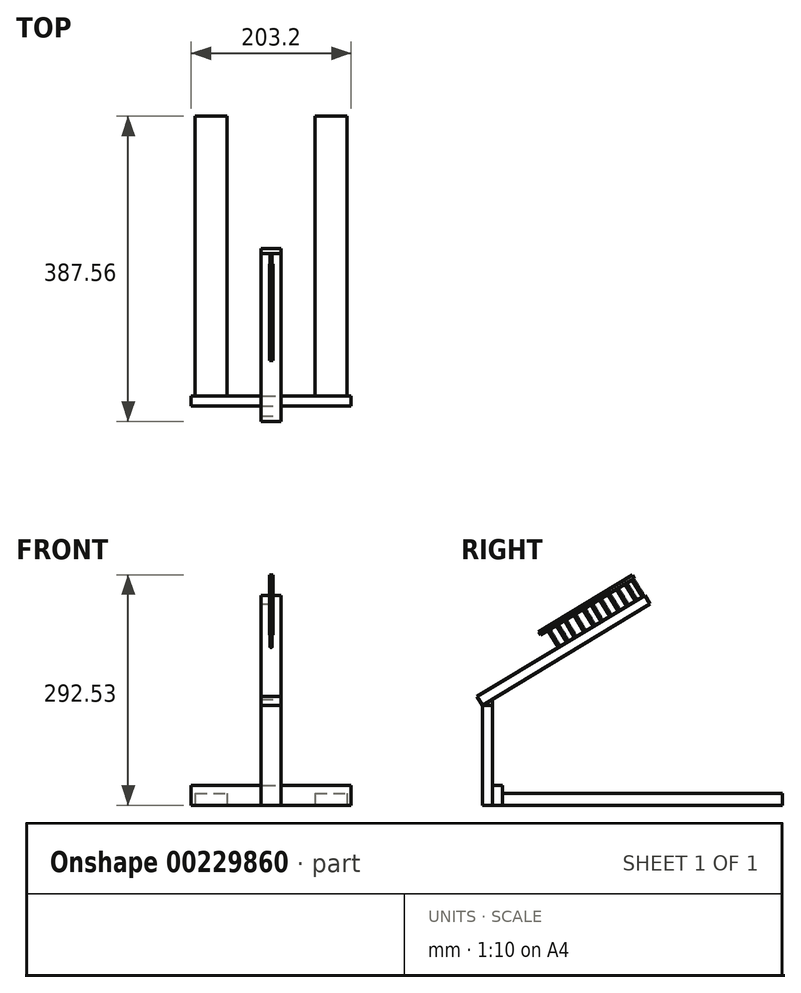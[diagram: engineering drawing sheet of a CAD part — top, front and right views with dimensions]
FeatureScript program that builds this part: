
annotation { "Feature Type Name" : "Feature", "Feature Type Description" : "" }
export const myFeature = defineFeature(function(context is Context, id is Id, definition is map)
    precondition{}
    {
        {
            var Q0;
            Q0=qCreatedBy(makeId("Top.planeOp"),FACE);
            var sketch = newSketch(context, id + "F0", { "sketchPlane" : qUnion([Q0])});
            skLineSegment(sketch, "E0.bottom", {"start": v(0, 0) * mm, "end": v(203.2, 0) * mm});
            skLineSegment(sketch, "E0.top", {"start": v(0, -12.7) * mm, "end": v(203.2, -12.7) * mm});
            skLineSegment(sketch, "E0.left", {"start": v(0, 0) * mm, "end": v(0, -12.7) * mm});
            skLineSegment(sketch, "E0.right", {"start": v(203.2, 0) * mm, "end": v(203.2, -12.7) * mm});
            skLineSegment(sketch, "E1.bottom", {"start": v(5.08, 355.6) * mm, "end": v(45.72, 355.6) * mm});
            skLineSegment(sketch, "E1.top", {"start": v(5.08, 0) * mm, "end": v(45.72, 0) * mm});
            skLineSegment(sketch, "E1.left", {"start": v(5.08, 355.6) * mm, "end": v(5.08, 0) * mm});
            skLineSegment(sketch, "E1.right", {"start": v(45.72, 355.6) * mm, "end": v(45.72, 0) * mm});
            skLineSegment(sketch, "E2.bottom", {"start": v(157.48, 355.6) * mm, "end": v(198.12, 355.6) * mm});
            skLineSegment(sketch, "E2.top", {"start": v(157.48, 0) * mm, "end": v(198.12, 0) * mm});
            skLineSegment(sketch, "E2.left", {"start": v(157.48, 355.6) * mm, "end": v(157.48, 0) * mm});
            skLineSegment(sketch, "E2.right", {"start": v(198.12, 355.6) * mm, "end": v(198.12, 0) * mm});
            skLineSegment(sketch, "E3.bottom", {"start": v(88.9, -12.7) * mm, "end": v(114.3, -12.7) * mm});
            skLineSegment(sketch, "E3.top", {"start": v(88.9, -25.4) * mm, "end": v(114.3, -25.4) * mm});
            skLineSegment(sketch, "E3.left", {"start": v(88.9, -12.7) * mm, "end": v(88.9, -25.4) * mm});
            skLineSegment(sketch, "E3.right", {"start": v(114.3, -12.7) * mm, "end": v(114.3, -25.4) * mm});
            skSolve(sketch);
        }
        {
            var Q0;
            Q0=qCreatedBy(makeId("Front.planeOp"),FACE);
            var sketch = newSketch(context, id + "F1", { "sketchPlane" : qUnion([Q0])});
            skLineSegment(sketch, "E4.bottom", {"start": v(0, 25.4) * mm, "end": v(203.2, 25.4) * mm});
            skLineSegment(sketch, "E4.top", {"start": v(0, 0) * mm, "end": v(203.2, 0) * mm});
            skLineSegment(sketch, "E4.left", {"start": v(0, 25.4) * mm, "end": v(0, 0) * mm});
            skLineSegment(sketch, "E4.right", {"start": v(203.2, 25.4) * mm, "end": v(203.2, 0) * mm});
            skSolve(sketch);
        }
        {
            var Q0;
            Q0=makeQuery(id+"F0.imprint","IMPRINT",FACE,{"disambiguationData":[TD([[makeQuery(id+"F0.imprint","IMPRINT",EDGE,{"derivedFrom":sQuery(id+"F0.wireOp",EDGE,"E2.bottom")}),-1.0]])]});
            var Q1;
            Q1=makeQuery(id+"F0.imprint","IMPRINT",FACE,{"disambiguationData":[TD([[makeQuery(id+"F0.imprint","IMPRINT",EDGE,{"derivedFrom":sQuery(id+"F0.wireOp",EDGE,"E1.bottom")}),-1.0]])]});
            extrude(context, id + "F2", {"entities" : qUnion([Q0, Q1]), "depth" : 15.24 * mm});
        }
        {
            var Q0;
            Q0=makeQuery(id+"F1.imprint","IMPRINT",FACE,{"disambiguationData":[TD([[makeQuery(id+"F1.imprint","IMPRINT",EDGE,{"derivedFrom":sQuery(id+"F1.wireOp",EDGE,"E4.bottom")}),-1.0]])]});
            extrude(context, id + "F3", {"entities" : qUnion([Q0]), "depth" : 12.7 * mm});
        }
        {
            var Q0;
            Q0=makeQuery(id+"F3.opExtrude","CAP_FACE",FACE,{"disambiguationData":[OSD([sQuery(id+"F1.wireOp",EDGE,"E4.bottom"),sQuery(id+"F1.wireOp",EDGE,"E4.top"),sQuery(id+"F1.wireOp",EDGE,"E4.left"),sQuery(id+"F1.wireOp",EDGE,"E4.right")])],"isStart":false});
            var sketch = newSketch(context, id + "F4", { "sketchPlane" : qUnion([Q0])});
            skLineSegment(sketch, "E5.bottom", {"start": v(88.9, 127) * mm, "end": v(114.3, 127) * mm});
            skLineSegment(sketch, "E5.top", {"start": v(88.9, 0) * mm, "end": v(114.3, 0) * mm});
            skLineSegment(sketch, "E5.left", {"start": v(88.9, 127) * mm, "end": v(88.9, 0) * mm});
            skLineSegment(sketch, "E5.right", {"start": v(114.3, 127) * mm, "end": v(114.3, 0) * mm});
            skSolve(sketch);
        }
        {
            var Q0;
            {var subQ0=sQuery(id+"F4.wireOp",EDGE,"E5.top");Q0=makeQuery(id+"F4.imprint","IMPRINT",FACE,{"disambiguationData":[TD([[makeQuery(id+"F4.imprint","IMPRINT",EDGE,{"derivedFrom":subQ0}),1.0]])]});}
            var Q1;
            {var subQ0=sQuery(id+"F4.wireOp",EDGE,"E5.bottom");Q1=makeQuery(id+"F4.imprint","IMPRINT",FACE,{"disambiguationData":[TD([[makeQuery(id+"F4.imprint","IMPRINT",EDGE,{"derivedFrom":subQ0}),-1.0]])]});}
            extrude(context, id + "F5", {"entities" : qUnion([Q0, Q1]), "operationType" : NewBodyOperationType.ADD, "depth" : 12.7 * mm});
        }
        {
            var Q0;
            Q0=makeQuery(id+"F5.opExtrude","SWEPT_FACE",FACE,{"disambiguationData":[OSD([sQuery(id+"F4.wireOp",EDGE,"E5.right")])]});
            var sketch = newSketch(context, id + "F6", { "sketchPlane" : qUnion([Q0])});
            skLineSegment(sketch, "E6.bottom", {"start": v(-31.96, 137.87) * mm, "end": v(181.14, 266.51) * mm});
            skLineSegment(sketch, "E6.top", {"start": v(-25.4, 127) * mm, "end": v(187.7, 255.64) * mm});
            skLineSegment(sketch, "E6.left", {"start": v(-31.96, 137.87) * mm, "end": v(-25.4, 127) * mm});
            skLineSegment(sketch, "E6.right", {"start": v(181.14, 266.51) * mm, "end": v(187.7, 255.64) * mm});
            skLineSegment(sketch, "E7", {"start": v(-12.7, 127) * mm, "end": v(-12.7, 134.67) * mm});
            skSolve(sketch);
        }
        {
            var Q0;
            Q0=makeQuery(id+"F6.imprint","IMPRINT",FACE,{"disambiguationData":[TD([[makeQuery(id+"F6.imprint","IMPRINT",EDGE,{"derivedFrom":sQuery(id+"F6.wireOp",EDGE,"E6.bottom")}),-1.0]])]});
            extrude(context, id + "F7", {"entities" : qUnion([Q0]), "oppositeDirection" : true, "depth" : 25.4 * mm});
        }
        {
            var Q0;
            Q0=makeQuery(id+"F5.opExtrude","SWEPT_FACE",FACE,{"disambiguationData":[OSD([sQuery(id+"F4.wireOp",EDGE,"E5.right")])]});
            var sketch = newSketch(context, id + "F8", { "sketchPlane" : qUnion([Q0])});
            skLineSegment(sketch, "E8", {"start": v(-12.7, 127) * mm, "end": v(-12.7, 134.67) * mm});
            skLineSegment(sketch, "E9", {"start": v(-12.7, 134.67) * mm, "end": v(-25.4, 127) * mm});
            skLineSegment(sketch, "E10", {"start": v(-25.4, 127) * mm, "end": v(-12.7, 127) * mm});
            skSolve(sketch);
        }
        {
            var Q0;
            Q0=makeQuery(id+"F8.imprint","IMPRINT",FACE,{"disambiguationData":[TD([[makeQuery(id+"F8.imprint","IMPRINT",EDGE,{"derivedFrom":sQuery(id+"F8.wireOp",EDGE,"E8")}),1.0]])]});
            extrude(context, id + "F9", {"entities" : qUnion([Q0]), "oppositeDirection" : true, "depth" : 25.4 * mm});
        }
        {
            var Q0;
            Q0=makeQuery(id+"F7.opExtrude","SWEPT_FACE",FACE,{"disambiguationData":[OSD([sQuery(id+"F6.wireOp",EDGE,"E6.bottom")])]});
            var sketch = newSketch(context, id + "F10", { "sketchPlane" : qUnion([Q0])});
            skCircle(sketch, "E11", {"center": v(101.6, 290.27) * mm, "radius": 1.27 * mm});
            skCircle(sketch, "E12", {"center": v(101.6, 267.4) * mm, "radius": 1.27 * mm});
            skCircle(sketch, "E13", {"center": v(101.6, 242) * mm, "radius": 1.27 * mm});
            skCircle(sketch, "E14", {"center": v(101.6, 217.88) * mm, "radius": 1.27 * mm});
            skCircle(sketch, "E15", {"center": v(101.6, 203.9) * mm, "radius": 1.27 * mm});
            skCircle(sketch, "E16", {"center": v(101.6, 189.94) * mm, "radius": 1.27 * mm});
            skCircle(sketch, "E17", {"center": v(101.6, 178.5) * mm, "radius": 1.27 * mm});
            skCircle(sketch, "E18", {"center": v(101.6, 165.8) * mm, "radius": 1.27 * mm});
            skCircle(sketch, "E19", {"center": v(101.6, 229.3) * mm, "radius": 1.27 * mm});
            skCircle(sketch, "E20", {"center": v(101.6, 254.7) * mm, "radius": 1.27 * mm});
            skCircle(sketch, "E21", {"center": v(101.6, 280.1) * mm, "radius": 1.27 * mm});
            skSolve(sketch);
        }
        {
            var Q0;
            Q0 = qSketchRegion(id + "F10", true);
            extrude(context, id + "F11", {"entities" : qUnion([Q0]), "operationType" : NewBodyOperationType.ADD, "depth" : 25.4 * mm});
        }
        {
            var Q0;
            Q0=makeQuery(id+"F11.opExtrude","CAP_FACE",FACE,{"disambiguationData":[OSD([sQuery(id+"F10.wireOp",EDGE,"E11")])],"isStart":false});
            var sketch = newSketch(context, id + "F12", { "sketchPlane" : qUnion([Q0])});
            skLineSegment(sketch, "E22.bottom", {"start": v(99.6, 152.97) * mm, "end": v(103.67, 152.97) * mm});
            skLineSegment(sketch, "E22.top", {"start": v(99.6, 292.67) * mm, "end": v(103.67, 292.67) * mm});
            skLineSegment(sketch, "E22.left", {"start": v(99.6, 292.67) * mm, "end": v(99.6, 152.97) * mm});
            skLineSegment(sketch, "E22.right", {"start": v(103.67, 292.67) * mm, "end": v(103.67, 152.97) * mm});
            skSolve(sketch);
        }
        {
            var Q0;
            Q0 = qSketchRegion(id + "F12", true);
            extrude(context, id + "F13", {"entities" : qUnion([Q0]), "operationType" : NewBodyOperationType.ADD, "depth" : 5.08 * mm});
        }
    });
